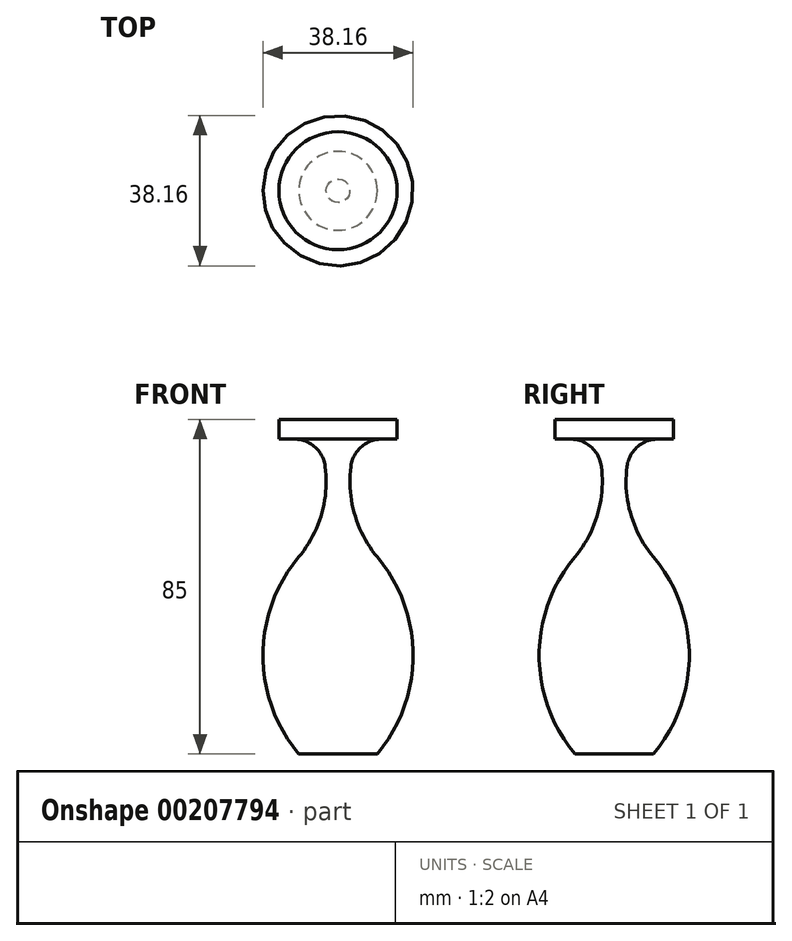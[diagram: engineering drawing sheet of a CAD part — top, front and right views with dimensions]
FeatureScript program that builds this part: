
annotation { "Feature Type Name" : "Feature", "Feature Type Description" : "" }
export const myFeature = defineFeature(function(context is Context, id is Id, definition is map)
    precondition{}
    {
        {
            var Q0;
            Q0=qCreatedBy(makeId("Front.planeOp"),FACE);
            var sketch = newSketch(context, id + "F0", { "sketchPlane" : qUnion([Q0])});
            skLineSegment(sketch, "E0", {"start": v(0, 0) * mm, "end": v(0, 80) * mm});
            skLineSegment(sketch, "E1", {"start": v(0, 0) * mm, "end": v(10, 0) * mm});
            skArc(sketch, "E2", {"start": v(10, 0) * mm, "mid": v(19.08, 25) * mm, "end": v(10, 50) * mm});
            skArc(sketch, "E3", {"start": v(5, 80) * mm, "mid": v(3.42, 64.32) * mm, "end": v(10, 50) * mm});
            skLineSegment(sketch, "E4", {"start": v(15, 80) * mm, "end": v(15, 85) * mm});
            skLineSegment(sketch, "E5", {"start": v(15, 85) * mm, "end": v(0, 85) * mm});
            skLineSegment(sketch, "E6", {"start": v(0, 85) * mm, "end": v(0, 80) * mm});
            skLineSegment(sketch, "E7", {"start": v(15, 80) * mm, "end": v(5, 80) * mm});
            skSolve(sketch);
        }
        {
            var Q0;
            Q0 = qSketchRegion(id + "F0", true);
            var Q1;
            Q1=sQuery(id+"F0.wireOp",EDGE,"E0");
            revolve(context, id + "F1", {"entities" : qUnion([Q0]), "axis" : qUnion([Q1]), "revolveType" : RevolveType.FULL});
        }
        {
            var Q0;
            Q0=makeQuery(id+"F1.opRevolve","SWEPT_EDGE",EDGE,{"disambiguationData":[OSD([sQuery(id+"F0.wireOp",EDGE,"E3"),sQuery(id+"F0.wireOp",EDGE,"tCd9H1ch-hhov-lTIr-XZBm-AJwywnV3BYZo")])]});
            fillet(context, id + "F2", {"entities" : qUnion([Q0]), "radius" : 8 * mm, "tangentPropagation" : true, "allowEdgeOverflow" : false});
        }
    });
